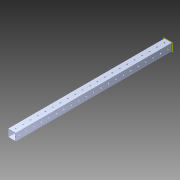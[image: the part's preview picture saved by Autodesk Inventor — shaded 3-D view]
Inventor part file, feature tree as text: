
AUTODESK INVENTOR PART (.ipt)
format: ipt  version: 2014 SP1 (Build 180222100, 222)  size: 1,239,552 bytes
history: native  units: in
note: dims shown in document units (in); Inventor stores cm internally (conversion verified against a paired STEP export)
features: pattern_circular x1, other x1, plane x1, extrude x1, imported_body x1, sketch x1
ambient origin geometry x8: Origin, YZ Plane, XZ Plane, XY Plane, X Axis, Y Axis, Z Axis, Center Point
bodies: Body1 (feature_tree)
feature tree (6):
  pattern_circular  "CirPattern2"
  other  "217-3426-STEP1"
  plane  "Work Plane1"
  extrude  "Extrusion1"  Depth=3937.0079in TaperAngle=0.0deg
  imported_body  "Base1"
  sketch  "Sketch1"  dims[d0=-21.0in d1=3937.0079in d2=0.0in]
